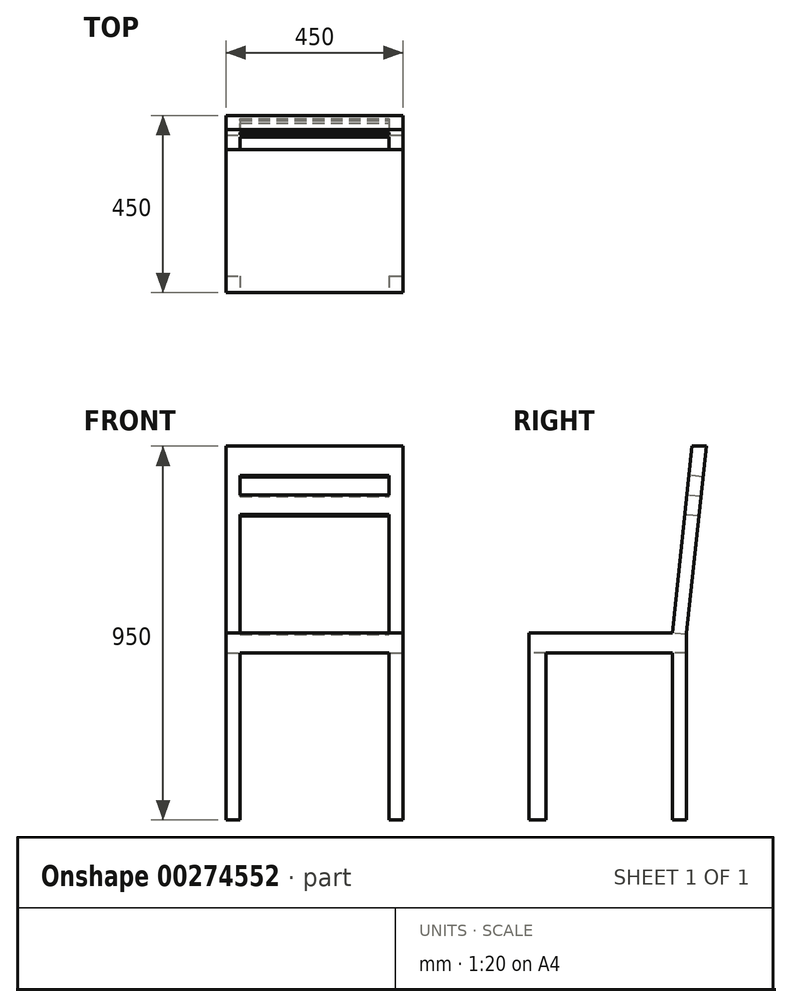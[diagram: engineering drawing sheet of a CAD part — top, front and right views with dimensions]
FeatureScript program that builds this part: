
annotation { "Feature Type Name" : "Feature", "Feature Type Description" : "" }
export const myFeature = defineFeature(function(context is Context, id is Id, definition is map)
    precondition{}
    {
        {
            var Q0;
            Q0=qCreatedBy(makeId("Top.planeOp"),FACE);
            var sketch = newSketch(context, id + "F0", { "sketchPlane" : qUnion([Q0])});
            skLineSegment(sketch, "E0.bottom", {"start": v(225, 225) * mm, "end": v(-225, 225) * mm});
            skLineSegment(sketch, "E0.top", {"start": v(225, -225) * mm, "end": v(-225, -225) * mm});
            skLineSegment(sketch, "E0.left", {"start": v(225, 225) * mm, "end": v(225, -225) * mm});
            skLineSegment(sketch, "E0.right", {"start": v(-225, 225) * mm, "end": v(-225, -225) * mm});
            skPoint(sketch, "E0.middle", {"position": v(0, 0) * mm});
            skSolve(sketch);
        }
        {
            var Q0;
            Q0=qSketchRegion(id+"F0",true);
            extrude(context, id + "F1", {"entities" : qUnion([Q0]), "depth" : 950 * mm});
        }
        {
            var Q0;
            Q0=makeQuery(id+"F1.opExtrude","SWEPT_FACE",FACE,{"disambiguationData":[OSD([sQuery(id+"F0.wireOp",EDGE,"E0.left")])]});
            var sketch = newSketch(context, id + "F2", { "sketchPlane" : qUnion([Q0])});
            skLineSegment(sketch, "E1.bottom", {"start": v(225, 475) * mm, "end": v(-225, 475) * mm});
            skLineSegment(sketch, "E1.top", {"start": v(225, 425) * mm, "end": v(-225, 425) * mm});
            skLineSegment(sketch, "E1.left", {"start": v(225, 475) * mm, "end": v(225, 425) * mm});
            skLineSegment(sketch, "E1.right", {"start": v(-225, 475) * mm, "end": v(-225, 425) * mm});
            skLineSegment(sketch, "E2", {"start": v(225, 950) * mm, "end": v(175, 475) * mm});
            skLineSegment(sketch, "E3", {"start": v(189, 950) * mm, "end": v(139, 475) * mm});
            skLineSegment(sketch, "E4", {"start": v(189, 950) * mm, "end": v(225, 950) * mm});
            skLineSegment(sketch, "E5", {"start": v(139, 475) * mm, "end": v(175, 475) * mm});
            skLineSegment(sketch, "E6", {"start": v(175, 475) * mm, "end": v(139, 475) * mm});
            skLineSegment(sketch, "E7", {"start": v(175, 475) * mm, "end": v(175, 0) * mm});
            skLineSegment(sketch, "E8", {"start": v(139, 475) * mm, "end": v(139, 0) * mm});
            skLineSegment(sketch, "E9", {"start": v(-182.66, 475) * mm, "end": v(-182.66, 0) * mm});
            skSolve(sketch);
        }
        {
            var Q0;
            {var subQ0=sQuery(id+"F2.wireOp",EDGE,"E1.left");Q0=makeQuery(id+"F2.imprint","IMPRINT",FACE,{"disambiguationData":[TD([[makeQuery(id+"F2.imprint","IMPRINT",EDGE,{"derivedFrom":subQ0}),-1.0]])]});}
            var Q1;
            {var subQ4=sQuery(id+"F2.wireOp",EDGE,"E3");Q1=makeQuery(id+"F2.imprint","IMPRINT",FACE,{"disambiguationData":[TD([[makeQuery(id+"F2.imprint","IMPRINT",EDGE,{"derivedFrom":subQ4}),-1.0]])]});}
            var Q2;
            {var subQ0=sQuery(id+"F2.wireOp",EDGE,"E8");var subQ1=sQuery(id+"F2.wireOp",EDGE,"E1.top");var subQ2=makeQuery(id+"F2.imprint","INTERSECT",VERTEX,{"derivedFrom":[subQ1,subQ0]});Q2=makeQuery(id+"F2.imprint","IMPRINT",FACE,{"disambiguationData":[TD([[makeQuery(id+"F2.imprint","IMPRINT",EDGE,{"disambiguationData":[TD([[subQ2,-1.0]])],"derivedFrom":subQ1}),1.0]])]});}
            var Q3;
            {var subQ1=sQuery(id+"F0.wireOp",EDGE,"E0.left");var subQ4=sQuery(id+"F2.wireOp",EDGE,"E7");var subQ6=makeQuery(id+"F1.opExtrude","CAP_EDGE",EDGE,{"disambiguationData":[OSD([subQ1])],"isStart":true});var subQ8=makeQuery(id+"F2.imprint","INTERSECT",VERTEX,{"derivedFrom":[subQ6,subQ4]});Q3=makeQuery(id+"F2.imprint","IMPRINT",FACE,{"disambiguationData":[TD([[makeQuery(id+"F2.imprint","IMPRINT",EDGE,{"disambiguationData":[TD([[subQ8,1.0]])],"derivedFrom":subQ4}),1.0]])]});}
            var Q4;
            {var subQ3=sQuery(id+"F2.wireOp",EDGE,"E2");Q4=makeQuery(id+"F2.imprint","IMPRINT",FACE,{"disambiguationData":[TD([[makeQuery(id+"F2.imprint","IMPRINT",EDGE,{"derivedFrom":subQ3}),1.0]])]});}
            extrude(context, id + "F3", {"entities" : qUnion([Q0, Q1, Q2, Q3, Q4]), "operationType" : NewBodyOperationType.REMOVE, "endBound" : BoundingType.THROUGH_ALL, "oppositeDirection" : true, "depth" : 25 * mm});
        }
        {
            var Q0;
            Q0=makeQuery(id+"F1.opExtrude","SWEPT_FACE",FACE,{"disambiguationData":[OSD([sQuery(id+"F0.wireOp",EDGE,"E0.top")])]});
            var sketch = newSketch(context, id + "F4", { "sketchPlane" : qUnion([Q0])});
            skLineSegment(sketch, "E10", {"start": v(-189, 0) * mm, "end": v(-189, 425) * mm});
            skLineSegment(sketch, "E11", {"start": v(-189, 425) * mm, "end": v(189, 425) * mm});
            skLineSegment(sketch, "E12", {"start": v(189, 425) * mm, "end": v(189, 0) * mm});
            skSolve(sketch);
        }
        {
            var Q0;
            {var subQ0=sQuery(id+"F4.wireOp",EDGE,"E10");Q0=makeQuery(id+"F4.imprint","IMPRINT",FACE,{"disambiguationData":[TD([[makeQuery(id+"F4.imprint","IMPRINT",EDGE,{"derivedFrom":subQ0}),-1.0]])]});}
            extrude(context, id + "F5", {"entities" : qUnion([Q0]), "operationType" : NewBodyOperationType.REMOVE, "endBound" : BoundingType.THROUGH_ALL, "oppositeDirection" : true, "depth" : 25 * mm});
        }
        {
            var Q0;
            Q0=makeQuery(id+"F3.boolean.opBoolean","COPY",FACE,{"derivedFrom":makeQuery(id+"F3.opExtrude","SWEPT_FACE",FACE,{"disambiguationData":[OSD([sQuery(id+"F2.wireOp",EDGE,"E3")])]})});
            var sketch = newSketch(context, id + "F6", { "sketchPlane" : qUnion([Q0])});
            skLineSegment(sketch, "E13", {"start": v(-189, 486.94) * mm, "end": v(-189, 889.57) * mm});
            skLineSegment(sketch, "E14", {"start": v(-189, 889.57) * mm, "end": v(189, 889.57) * mm});
            skLineSegment(sketch, "E15", {"start": v(189, 889.57) * mm, "end": v(189, 486.94) * mm});
            skLineSegment(sketch, "E16", {"start": v(-189, 839.57) * mm, "end": v(189, 839.57) * mm});
            skLineSegment(sketch, "E17", {"start": v(-189, 789.57) * mm, "end": v(189, 789.57) * mm});
            skSolve(sketch);
        }
        {
            var Q0;
            {var subQ0=sQuery(id+"F6.wireOp",EDGE,"E14");Q0=makeQuery(id+"F6.imprint","IMPRINT",FACE,{"disambiguationData":[TD([[makeQuery(id+"F6.imprint","IMPRINT",EDGE,{"derivedFrom":subQ0}),-1.0]])]});}
            var Q1;
            {var subQ3=sQuery(id+"F6.wireOp",EDGE,"E17");Q1=makeQuery(id+"F6.imprint","IMPRINT",FACE,{"disambiguationData":[TD([[makeQuery(id+"F6.imprint","IMPRINT",EDGE,{"derivedFrom":subQ3}),-1.0]])]});}
            extrude(context, id + "F7", {"entities" : qUnion([Q0, Q1]), "operationType" : NewBodyOperationType.REMOVE, "endBound" : BoundingType.THROUGH_ALL, "oppositeDirection" : true, "depth" : 25 * mm});
        }
    });
